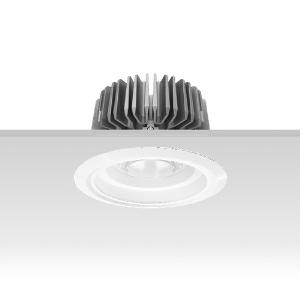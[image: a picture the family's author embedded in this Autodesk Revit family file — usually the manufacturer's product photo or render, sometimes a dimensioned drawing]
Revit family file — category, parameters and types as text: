
# Revit family: 3f_filippi_-_3f_reno_bianco_ampio_3f_filippi_-_30387_a01023_-_3f_reno_150_wh_3000-930_dali_wide___vt_wh_fdca
name_source: partatom
category: Lighting Fixtures
units: mm (PartAtom-declared; Revit-internal decimal feet)

## family parameters
Cut with Voids When Loaded = No
Host = Face
Light Source = No
Part Type = Normal
Room Calculation Point = No
Round Connector Dimension = Use Diameter
Shared = No

## types (1)
- 3F Filippi - 3F Reno Bianco Ampio (1 x LED, 2656 lm, 37 W, 3000 K)
    Apparent Load = 37 VA
    Approval mark = CE
    CIE Flux Codes = 74 93 99 100 100
    Color Rendering = 90
    Color Temperature = 3000 K
    Control Gear = Electronic transformer
    Default Elevation = 1800 mm
    Description = ILLUMINOTECHNICAL
Luminous efficiency 100% (DLOR 100%, ULOR 0%).
Initial luminous flux of the luminaire 2656 lm.
Direct symmetric wide distribution.
Installation Interdistance Transv.D = 1.54 x hu - Long.D = 1.54 x hu.
Tabular UGR (CIE 117 - 4H-8H; S=0.25H; 70/50/20): RUG 24.4 - 24.2.
Beam angle: 74° - 73°.
Luminous efficacy 72 lm/W.
Lifetime (L90/B10): 30000 h. (tq+25°C)
Lifetime (L85/B10): 50000 h. (tq+25°C)
Lifetime (L70/B10): 80000 h. (tq+25°C)
Sudden decreased luminous flux after 50000 hours: 0% (C0).
Photobiological safety in compliance with IEC/TR 62778: RG0 risk exempt, (IEC 62471).
In compliance with IEC/EN 62722-2-1 - IEC/EN 62717 standards.

SOURCE
Compact LED module 3000/930.
Energy efficiency class (UE 2019/2020 - UE 2019/2015): F.
CIE 13.3 Colour rendering index: CRI >90 (R9 >50%).
IES TM-30 Fidelity Index: Rf = 92 Rg = 101.
CCT nominal colour temperature 3000 K.
Colour initial tolerance (MacAdam): SDCM 3.
Zhaga Book 3 compliant.

MECHANICAL
Passive heat dissipator in die-casting aluminium, oversized, for optimum thermal management of the LED module.
Parabolic element with graduated/concentric rings in white polycarbonate.
Transparent external lens with glossy and satin differentiated surfaces, with a cooling and anti-insect system in methacrylate (PMMA).
Fastening spring clips in stainless steel.
Dimensions: diameter 176 mm, height 111 mm. Weight 1.51 kg.
IP44 protection degree for exposed part, IP20 for recessed part.
Mechanical strength to impacts IK06 (1 joule).
Glow-wire test resistance 650°C.

ELECTRICAL
Wiring on a separate unit.
Halogen Free DALI-2 DATI (Parts 251, 252, 253), PUSH-DIM, electronic wiring 230V-50/60Hz, power factor 0.97 at full load, THD <25%, constant output current, SELV, class II, 1 driver, 1 DALI addresse.
Power of the luminaire 37 W.
ENEC - CE.
SAFE FLICKER: PstLM=<1 and SVM=<0.4 (IEC TR 61547-1 and IEC TR 63158), to ensure a more comfortable and safe light.
Luminaire compliant with EN 60598-2-22 for power supply from a centralised emergency system CPSS (Central Power Supply System), not incorporated in the luminaire - high risk areas excluded. The default power and flux are 100% in AC and 100% in DC.
Ambient temperature from 0°C to +25°C.
Temperature class T6 max 85°C.
Relative humidity UR: <85%.

INSTALLATION
Pull-up recessed fitting.
False ceiling carving: 150 mm.
All accessories dedicated to this product are available on the Catalog and on our website www.3F-Filippi.com.

ACCESSORIES
A01023 - VT transparent glass, tempered, not flammable, locked and in line with the trim, in white polycarbonate.

APPLICATIONS
Environments: architectural, commercial, exhibition areas, transit areas, corridors, shops, display windows, service areas.
In false ceilings with narrow voids.

LIGHT MANAGEMENT
Recommended minimum setting: 10%.
The luminaire, equipped with (DALI-2 DATI) driver, can be controlled manually with 3F Easy Dim technology or automatically/manually with wired or wireless DALI/D2D control systems.
The D2D driver guarantees interoperability with other devices with the same certification by making the following information available:
Device Data (Part 251), Energy Report (Part 252), Diagnosis & Maintenance (Part 253).
In electrical systems without a regulation system (manual or automatic) and DALI bus, a suitable jumper must be made on the DA-DA terminals of the appliance.

WARNING
Luminaire designed for disposal/recycling at end-of-life.
Replaceable (LED only) light source by a professional. Replaceable control gear by a professional.
    Height = 0 mm  [stored 0 ft]
    Lamp = 1 x LED
    Lamp Light Flux = 2656 lm
    Lamp Power = 37 W
    Lamp count = 1
    Length = 176 mm
    Lifetime = 50000 h
    Luminous efficacy = 72 lm/W
    Manufacturer = 3F Filippi
    ModVariant = No
    Model = 3F Filippi - 30387+A01023 - 3F Reno 150 WH 3000-930 DALI WIDE + VT WH
    Mounting Place = Ceiling
    Mounting Type = Recessed
    Number of Poles = 1
    OnlyDefault = Yes
    Power Factor = 1
    Product Name = 3F Filippi - 3F Reno Bianco Ampio
    Product group = recessed luminaire
    ProductGroupID = 4
    Protection Class = Protection class II
    Protection Degree = IP 20
    RLX_Detail_Level = 1
    RLX_Emergency_Light_Flux = 0 lm
    RLX_Emergency_Type = 0
    RLX_Emergency_Type_DB = No
    RlxData = <blob elided: 87445 chars, md5=723388ca>
    Socket = socket
    Standby Power = 0 W
    System Light Flux = 2656 lm
    System Power = 37 W
    Type Comments = Product without accessories
    Type Image = 3ffilippi_3f_reno_150_wh_d150__a01023.jpg
    URL = http://relux.com
    VarID = ---
    Voltage = 0 V
    Weight = 0.00 kg
    Width = 0 mm  [stored 0 ft]

note: [stored X ft] marks values corroborated as IEEE doubles in the binary element streams (Revit-internal decimal feet)

## geometry (parser evidence)
native form markers: Blend x4, Sweep x12
no freeform markers — native parametric forms only
